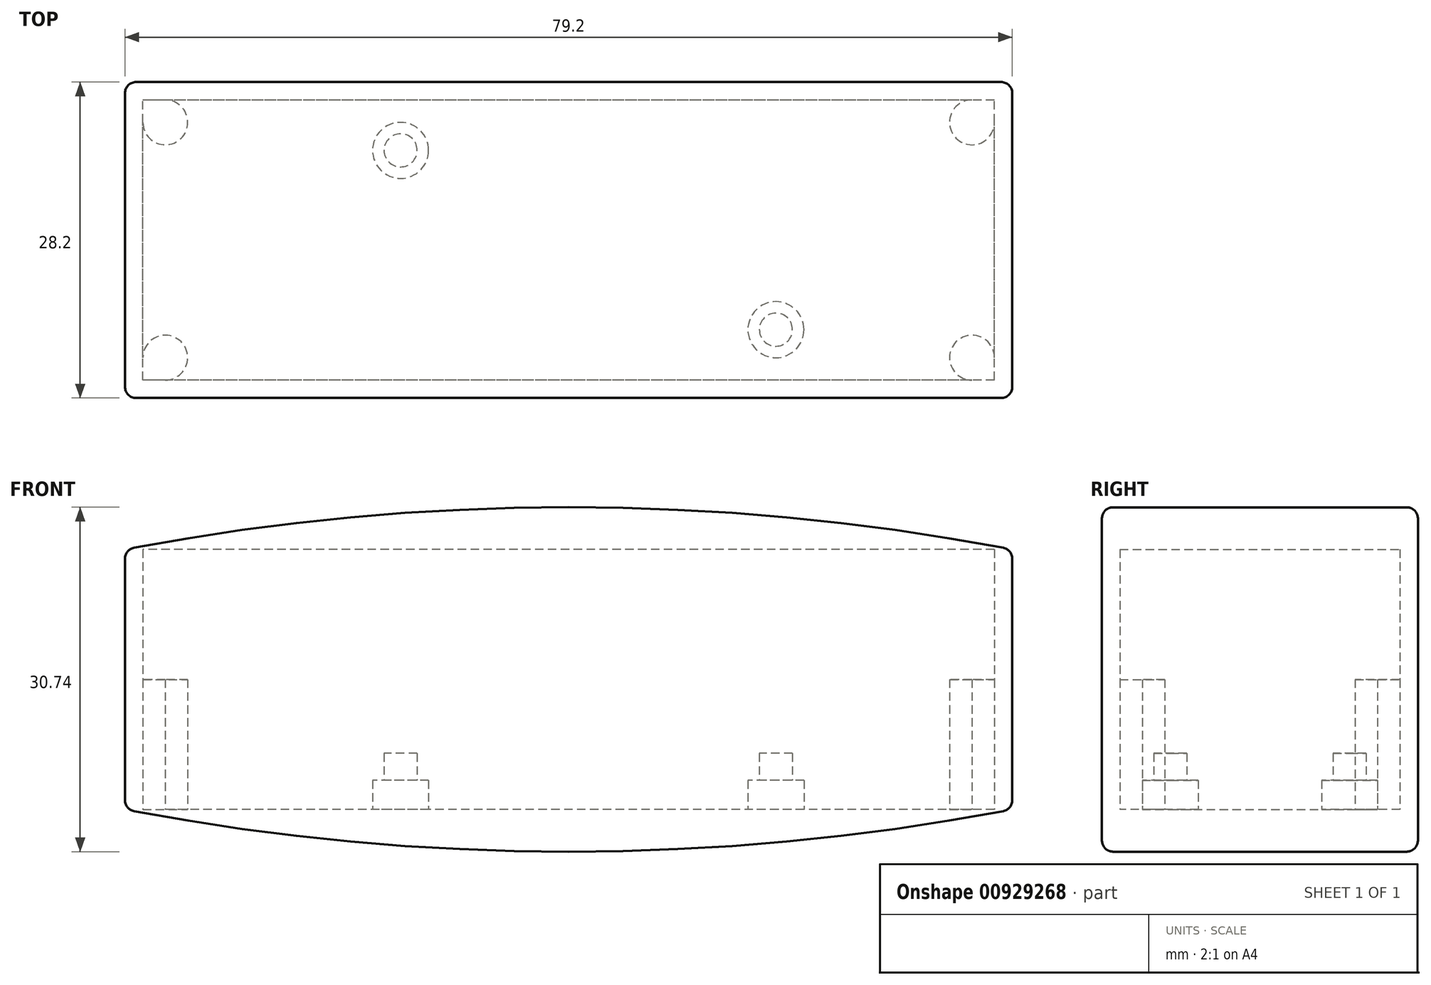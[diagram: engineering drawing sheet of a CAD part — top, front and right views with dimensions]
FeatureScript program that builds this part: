
annotation { "Feature Type Name" : "Feature", "Feature Type Description" : "" }
export const myFeature = defineFeature(function(context is Context, id is Id, definition is map)
    precondition{}
    {
        {
            var Q0;
            Q0=qCreatedBy(makeId("Top.planeOp"),FACE);
            var sketch = newSketch(context, id + "F0", { "sketchPlane" : qUnion([Q0])});
            skLineSegment(sketch, "E0.bottom", {"start": v(38, -12.5) * mm, "end": v(-38, -12.5) * mm});
            skLineSegment(sketch, "E0.top", {"start": v(38, 12.5) * mm, "end": v(-38, 12.5) * mm});
            skLineSegment(sketch, "E0.left", {"start": v(38, -12.5) * mm, "end": v(38, 12.5) * mm});
            skLineSegment(sketch, "E0.right", {"start": v(-38, -12.5) * mm, "end": v(-38, 12.5) * mm});
            skPoint(sketch, "E0.middle", {"position": v(0, 0) * mm});
            skLineSegment(sketch, "E1.0", {"start": v(39.6, 14.1) * mm, "end": v(-39.6, 14.1) * mm});
            skLineSegment(sketch, "E1.1", {"start": v(39.6, -14.1) * mm, "end": v(39.6, 14.1) * mm});
            skLineSegment(sketch, "E1.2", {"start": v(39.6, -14.1) * mm, "end": v(-39.6, -14.1) * mm});
            skLineSegment(sketch, "E1.3", {"start": v(-39.6, -14.1) * mm, "end": v(-39.6, 14.1) * mm});
            skCircle(sketch, "E2", {"center": v(-15, 8) * mm, "radius": 1.48 * mm});
            skCircle(sketch, "E3", {"center": v(18.5, -8) * mm, "radius": 1.48 * mm});
            skCircle(sketch, "E4", {"center": v(-15, 8) * mm, "radius": 2.5 * mm});
            skCircle(sketch, "E5", {"center": v(18.5, -8) * mm, "radius": 2.5 * mm});
            skCircle(sketch, "E6", {"center": v(-36, 10.5) * mm, "radius": 2 * mm});
            skCircle(sketch, "E7", {"center": v(-36, -10.5) * mm, "radius": 2 * mm});
            skCircle(sketch, "E8", {"center": v(36, 10.5) * mm, "radius": 2 * mm});
            skCircle(sketch, "E9", {"center": v(36, -10.5) * mm, "radius": 2 * mm});
            skSolve(sketch);
        }
        {
            var Q0;
            Q0=makeQuery(id+"F0.imprint","IMPRINT",FACE,{"disambiguationData":[TD([[makeQuery(id+"F0.imprint","IMPRINT",EDGE,{"derivedFrom":sQuery(id+"F0.wireOp",EDGE,"E2")}),1.0]])]});
            var Q1;
            Q1=makeQuery(id+"F0.imprint","IMPRINT",FACE,{"disambiguationData":[TD([[makeQuery(id+"F0.imprint","IMPRINT",EDGE,{"derivedFrom":sQuery(id+"F0.wireOp",EDGE,"E3")}),1.0]])]});
            extrude(context, id + "F1", {"entities" : qUnion([Q0, Q1]), "depth" : 5 * mm, "offsetDistance" : 25 * mm});
        }
        {
            var Q0;
            Q0=makeQuery(id+"F0.imprint","IMPRINT",FACE,{"disambiguationData":[TD([[makeQuery(id+"F0.imprint","IMPRINT",EDGE,{"derivedFrom":sQuery(id+"F0.wireOp",EDGE,"E3")}),-1.0]])]});
            var Q1;
            Q1=makeQuery(id+"F0.imprint","IMPRINT",FACE,{"disambiguationData":[TD([[makeQuery(id+"F0.imprint","IMPRINT",EDGE,{"derivedFrom":sQuery(id+"F0.wireOp",EDGE,"E2")}),-1.0]])]});
            extrude(context, id + "F2", {"entities" : qUnion([Q0, Q1]), "depth" : 2.6 * mm, "offsetDistance" : 25 * mm});
        }
        {
            var Q0;
            Q0=makeQuery(id+"F0.imprint","IMPRINT",FACE,{"disambiguationData":[TD([[makeQuery(id+"F0.imprint","IMPRINT",EDGE,{"derivedFrom":sQuery(id+"F0.wireOp",EDGE,"E0.bottom")}),1.0]])]});
            extrude(context, id + "F3", {"entities" : qUnion([Q0]), "depth" : 23.2 * mm, "offsetDistance" : 25 * mm});
        }
        {
            var Q0;
            {var subQ0=sQuery(id+"F0.wireOp",EDGE,"E6");var subQ1=makeQuery(id+"F0.imprint","INTERSECT",VERTEX,{"derivedFrom":[sQuery(id+"F0.wireOp",EDGE,"E0.top"),subQ0]});Q0=makeQuery(id+"F0.imprint","IMPRINT",FACE,{"disambiguationData":[TD([[makeQuery(id+"F0.imprint","IMPRINT",EDGE,{"disambiguationData":[TD([[subQ1,-1.0]])],"derivedFrom":subQ0}),1.0]])]});}
            var Q1;
            {var subQ0=sQuery(id+"F0.wireOp",EDGE,"E7");var subQ1=makeQuery(id+"F0.imprint","INTERSECT",VERTEX,{"derivedFrom":[sQuery(id+"F0.wireOp",EDGE,"E0.bottom"),subQ0]});Q1=makeQuery(id+"F0.imprint","IMPRINT",FACE,{"disambiguationData":[TD([[makeQuery(id+"F0.imprint","IMPRINT",EDGE,{"disambiguationData":[TD([[subQ1,1.0]])],"derivedFrom":subQ0}),1.0]])]});}
            var Q2;
            {var subQ0=sQuery(id+"F0.wireOp",EDGE,"E8");var subQ1=makeQuery(id+"F0.imprint","INTERSECT",VERTEX,{"derivedFrom":[sQuery(id+"F0.wireOp",EDGE,"E0.top"),subQ0]});Q2=makeQuery(id+"F0.imprint","IMPRINT",FACE,{"disambiguationData":[TD([[makeQuery(id+"F0.imprint","IMPRINT",EDGE,{"disambiguationData":[TD([[subQ1,1.0]])],"derivedFrom":subQ0}),1.0]])]});}
            var Q3;
            {var subQ0=sQuery(id+"F0.wireOp",EDGE,"E0.right");var subQ1=sQuery(id+"F0.wireOp",EDGE,"E0.top");var subQ2=makeQuery(id+"F0.imprint","INTERSECT",VERTEX,{"derivedFrom":[subQ1,subQ0]});Q3=makeQuery(id+"F0.imprint","IMPRINT",FACE,{"disambiguationData":[TD([[makeQuery(id+"F0.imprint","IMPRINT",EDGE,{"disambiguationData":[TD([[subQ2,1.0]])],"derivedFrom":subQ1}),1.0]])]});}
            var Q4;
            {var subQ0=sQuery(id+"F0.wireOp",EDGE,"E0.left");var subQ1=sQuery(id+"F0.wireOp",EDGE,"E0.top");var subQ2=makeQuery(id+"F0.imprint","INTERSECT",VERTEX,{"derivedFrom":[subQ1,subQ0]});Q4=makeQuery(id+"F0.imprint","IMPRINT",FACE,{"disambiguationData":[TD([[makeQuery(id+"F0.imprint","IMPRINT",EDGE,{"disambiguationData":[TD([[subQ2,-1.0]])],"derivedFrom":subQ1}),1.0]])]});}
            var Q5;
            {var subQ0=sQuery(id+"F0.wireOp",EDGE,"E9");var subQ1=makeQuery(id+"F0.imprint","INTERSECT",VERTEX,{"derivedFrom":[sQuery(id+"F0.wireOp",EDGE,"E0.bottom"),subQ0]});Q5=makeQuery(id+"F0.imprint","IMPRINT",FACE,{"disambiguationData":[TD([[makeQuery(id+"F0.imprint","IMPRINT",EDGE,{"disambiguationData":[TD([[subQ1,1.0]])],"derivedFrom":subQ0}),1.0]])]});}
            var Q6;
            {var subQ0=sQuery(id+"F0.wireOp",EDGE,"E0.right");var subQ1=sQuery(id+"F0.wireOp",EDGE,"E0.bottom");var subQ2=makeQuery(id+"F0.imprint","INTERSECT",VERTEX,{"derivedFrom":[subQ1,subQ0]});Q6=makeQuery(id+"F0.imprint","IMPRINT",FACE,{"disambiguationData":[TD([[makeQuery(id+"F0.imprint","IMPRINT",EDGE,{"disambiguationData":[TD([[subQ2,1.0]])],"derivedFrom":subQ1}),-1.0]])]});}
            var Q7;
            {var subQ0=sQuery(id+"F0.wireOp",EDGE,"E0.left");var subQ1=sQuery(id+"F0.wireOp",EDGE,"E0.bottom");var subQ2=makeQuery(id+"F0.imprint","INTERSECT",VERTEX,{"derivedFrom":[subQ1,subQ0]});Q7=makeQuery(id+"F0.imprint","IMPRINT",FACE,{"disambiguationData":[TD([[makeQuery(id+"F0.imprint","IMPRINT",EDGE,{"disambiguationData":[TD([[subQ2,-1.0]])],"derivedFrom":subQ1}),-1.0]])]});}
            extrude(context, id + "F4", {"entities" : qUnion([Q0, Q1, Q2, Q3, Q4, Q5, Q6, Q7]), "depth" : 11.6 * mm, "offsetDistance" : 25 * mm});
        }
        {
            var Q0;
            Q0=makeQuery(id+"F3.opExtrude","SWEPT_FACE",FACE,{"disambiguationData":[OSD([sQuery(id+"F0.wireOp",EDGE,"E1.2")])]});
            var sketch = newSketch(context, id + "F5", { "sketchPlane" : qUnion([Q0])});
            skLineSegment(sketch, "E10.0", {"start": v(39.6, 23.2) * mm, "end": v(-39.6, 23.2) * mm});
            skArc(sketch, "E11", {"start": v(39.6, 23.2) * mm, "mid": v(0, 26.97) * mm, "end": v(-39.6, 23.2) * mm});
            skSolve(sketch);
        }
        {
            var Q0;
            Q0=makeQuery(id+"F3.opExtrude","SWEPT_FACE",FACE,{"disambiguationData":[OSD([sQuery(id+"F0.wireOp",EDGE,"E1.2")])]});
            var sketch = newSketch(context, id + "F6", { "sketchPlane" : qUnion([Q0])});
            skLineSegment(sketch, "E12.0", {"start": v(39.6, 0) * mm, "end": v(-39.6, 0) * mm});
            skArc(sketch, "E13", {"start": v(-39.6, 0) * mm, "mid": v(0, -3.77) * mm, "end": v(39.6, 0) * mm});
            skSolve(sketch);
        }
        {
            var Q0;
            Q0 = qSketchRegion(id + "F5", true);
            var Q1;
            Q1=makeQuery(id+"F3.opExtrude","SWEPT_FACE",FACE,{"disambiguationData":[OSD([sQuery(id+"F0.wireOp",EDGE,"E1.0")])]});
            extrude(context, id + "F7", {"entities" : qUnion([Q0]), "operationType" : NewBodyOperationType.ADD, "endBound" : BoundingType.UP_TO_SURFACE, "oppositeDirection" : true, "depth" : 25 * mm, "endBoundEntityFace" : qUnion([Q1]), "offsetDistance" : 25 * mm});
        }
        {
            var Q0;
            Q0=makeQuery(id+"F6.imprint","IMPRINT",FACE,{"disambiguationData":[TD([[makeQuery(id+"F6.imprint","IMPRINT",EDGE,{"derivedFrom":sQuery(id+"F6.wireOp",EDGE,"E12.0")}),1.0]])]});
            var Q1;
            Q1=makeQuery(id+"F3.opExtrude","SWEPT_FACE",FACE,{"disambiguationData":[OSD([sQuery(id+"F0.wireOp",EDGE,"E1.0")])]});
            extrude(context, id + "F8", {"entities" : qUnion([Q0]), "operationType" : NewBodyOperationType.ADD, "endBound" : BoundingType.UP_TO_SURFACE, "oppositeDirection" : true, "depth" : 25 * mm, "endBoundEntityFace" : qUnion([Q1]), "offsetDistance" : 25 * mm});
        }
        {
            assignVariable(context, id + "F9", {"name" : "fillet", "anyValue" : 1});
        }
        {
            var Q0;
            Q0=makeQuery(id+"F3.opExtrude","SWEPT_EDGE",EDGE,{"disambiguationData":[OSD([sQuery(id+"F0.wireOp",EDGE,"E1.0"),sQuery(id+"F0.wireOp",EDGE,"E1.3")])]});
            var Q1;
            Q1=makeQuery(id+"F3.opExtrude","SWEPT_EDGE",EDGE,{"disambiguationData":[OSD([sQuery(id+"F0.wireOp",EDGE,"E1.2"),sQuery(id+"F0.wireOp",EDGE,"E1.3")])]});
            var Q2;
            Q2=makeQuery(id+"F3.opExtrude","SWEPT_EDGE",EDGE,{"disambiguationData":[OSD([sQuery(id+"F0.wireOp",EDGE,"E1.0"),sQuery(id+"F0.wireOp",EDGE,"E1.1")])]});
            var Q3;
            Q3=makeQuery(id+"F3.opExtrude","SWEPT_EDGE",EDGE,{"disambiguationData":[OSD([sQuery(id+"F0.wireOp",EDGE,"E1.1"),sQuery(id+"F0.wireOp",EDGE,"E1.2")])]});
            var Q4;
            {var subQ0=sQuery(id+"F0.wireOp",EDGE,"E1.1");Q4=makeQuery(id+"F8.boolean.opBoolean","MERGE",EDGE,{"derivedFrom":[makeQuery(id+"F3.opExtrude","CAP_EDGE",EDGE,{"disambiguationData":[OSD([subQ0])],"isStart":true}),makeQuery(id+"F8.opExtrude","SWEPT_EDGE",EDGE,{"disambiguationData":[OSD([subQ0,sQuery(id+"F0.wireOp",EDGE,"E1.2"),sQuery(id+"F6.wireOp",EDGE,"E12.0"),sQuery(id+"F6.wireOp",EDGE,"E13")])]})]});}
            var Q5;
            Q5=makeQuery(id+"F8.opExtrude","CAP_EDGE",EDGE,{"disambiguationData":[OSD([sQuery(id+"F6.wireOp",EDGE,"E13")])],"isStart":false});
            var Q6;
            {var subQ0=sQuery(id+"F0.wireOp",EDGE,"E1.3");Q6=makeQuery(id+"F8.boolean.opBoolean","MERGE",EDGE,{"derivedFrom":[makeQuery(id+"F3.opExtrude","CAP_EDGE",EDGE,{"disambiguationData":[OSD([subQ0])],"isStart":true}),makeQuery(id+"F8.opExtrude","SWEPT_EDGE",EDGE,{"disambiguationData":[OSD([sQuery(id+"F0.wireOp",EDGE,"E1.2"),subQ0,sQuery(id+"F6.wireOp",EDGE,"E12.0"),sQuery(id+"F6.wireOp",EDGE,"E13")])]})]});}
            var Q7;
            Q7=makeQuery(id+"F8.opExtrude","CAP_EDGE",EDGE,{"disambiguationData":[OSD([sQuery(id+"F6.wireOp",EDGE,"E13")])],"isStart":true});
            fillet(context, id + "F10", {"entities" : qUnion([Q0, Q1, Q2, Q3, Q4, Q5, Q6, Q7]), "radius" : (getVariable(context, 'fillet')) * mm, "tangentPropagation" : true, "allowEdgeOverflow" : false});
        }
        {
            var Q0;
            Q0=makeQuery(id+"F7.opExtrude","CAP_EDGE",EDGE,{"disambiguationData":[OSD([sQuery(id+"F5.wireOp",EDGE,"E11")])],"isStart":true});
            var Q1;
            Q1=makeQuery(id+"F10.opFillet","BLEND_EDGE",EDGE,{"blendedFrom":[makeQuery(id+"F3.opExtrude","SWEPT_EDGE",EDGE,{"disambiguationData":[OSD([sQuery(id+"F0.wireOp",EDGE,"E1.1"),sQuery(id+"F0.wireOp",EDGE,"E1.2")])]}),makeQuery(id+"F7.opExtrude","SWEPT_FACE",FACE,{"disambiguationData":[OSD([sQuery(id+"F5.wireOp",EDGE,"E11")])]})],"blendedInto":[makeQuery(id+"F7.opExtrude","SWEPT_FACE",FACE,{"disambiguationData":[OSD([sQuery(id+"F5.wireOp",EDGE,"E11")])]})]});
            var Q2;
            {var subQ0=sQuery(id+"F0.wireOp",EDGE,"E1.1");Q2=makeQuery(id+"F7.boolean.opBoolean","MERGE",EDGE,{"derivedFrom":[makeQuery(id+"F3.opExtrude","CAP_EDGE",EDGE,{"disambiguationData":[OSD([subQ0])],"isStart":false}),makeQuery(id+"F7.opExtrude","SWEPT_EDGE",EDGE,{"disambiguationData":[OSD([subQ0,sQuery(id+"F0.wireOp",EDGE,"E1.2"),sQuery(id+"F5.wireOp",EDGE,"E10.0"),sQuery(id+"F5.wireOp",EDGE,"E11")])]})]});}
            var Q3;
            Q3=makeQuery(id+"F10.opFillet","BLEND_EDGE",EDGE,{"blendedFrom":[makeQuery(id+"F3.opExtrude","SWEPT_EDGE",EDGE,{"disambiguationData":[OSD([sQuery(id+"F0.wireOp",EDGE,"E1.0"),sQuery(id+"F0.wireOp",EDGE,"E1.1")])]}),makeQuery(id+"F7.opExtrude","SWEPT_FACE",FACE,{"disambiguationData":[OSD([sQuery(id+"F5.wireOp",EDGE,"E11")])]})],"blendedInto":[makeQuery(id+"F7.opExtrude","SWEPT_FACE",FACE,{"disambiguationData":[OSD([sQuery(id+"F5.wireOp",EDGE,"E11")])]})]});
            var Q4;
            Q4=makeQuery(id+"F7.opExtrude","CAP_EDGE",EDGE,{"disambiguationData":[OSD([sQuery(id+"F5.wireOp",EDGE,"E11")])],"isStart":false});
            var Q5;
            Q5=makeQuery(id+"F10.opFillet","BLEND_EDGE",EDGE,{"blendedFrom":[makeQuery(id+"F3.opExtrude","SWEPT_EDGE",EDGE,{"disambiguationData":[OSD([sQuery(id+"F0.wireOp",EDGE,"E1.0"),sQuery(id+"F0.wireOp",EDGE,"E1.3")])]}),makeQuery(id+"F7.opExtrude","SWEPT_FACE",FACE,{"disambiguationData":[OSD([sQuery(id+"F5.wireOp",EDGE,"E11")])]})],"blendedInto":[makeQuery(id+"F7.opExtrude","SWEPT_FACE",FACE,{"disambiguationData":[OSD([sQuery(id+"F5.wireOp",EDGE,"E11")])]})]});
            var Q6;
            {var subQ0=sQuery(id+"F0.wireOp",EDGE,"E1.3");Q6=makeQuery(id+"F7.boolean.opBoolean","MERGE",EDGE,{"derivedFrom":[makeQuery(id+"F3.opExtrude","CAP_EDGE",EDGE,{"disambiguationData":[OSD([subQ0])],"isStart":false}),makeQuery(id+"F7.opExtrude","SWEPT_EDGE",EDGE,{"disambiguationData":[OSD([sQuery(id+"F0.wireOp",EDGE,"E1.2"),subQ0,sQuery(id+"F5.wireOp",EDGE,"E10.0"),sQuery(id+"F5.wireOp",EDGE,"E11")])]})]});}
            var Q7;
            Q7=makeQuery(id+"F10.opFillet","BLEND_EDGE",EDGE,{"blendedFrom":[makeQuery(id+"F3.opExtrude","SWEPT_EDGE",EDGE,{"disambiguationData":[OSD([sQuery(id+"F0.wireOp",EDGE,"E1.2"),sQuery(id+"F0.wireOp",EDGE,"E1.3")])]}),makeQuery(id+"F7.opExtrude","SWEPT_FACE",FACE,{"disambiguationData":[OSD([sQuery(id+"F5.wireOp",EDGE,"E11")])]})],"blendedInto":[makeQuery(id+"F7.opExtrude","SWEPT_FACE",FACE,{"disambiguationData":[OSD([sQuery(id+"F5.wireOp",EDGE,"E11")])]})]});
            fillet(context, id + "F11", {"entities" : qUnion([Q0, Q1, Q2, Q3, Q4, Q5, Q6, Q7]), "radius" : 1 * mm, "tangentPropagation" : true, "allowEdgeOverflow" : false});
        }
    });
